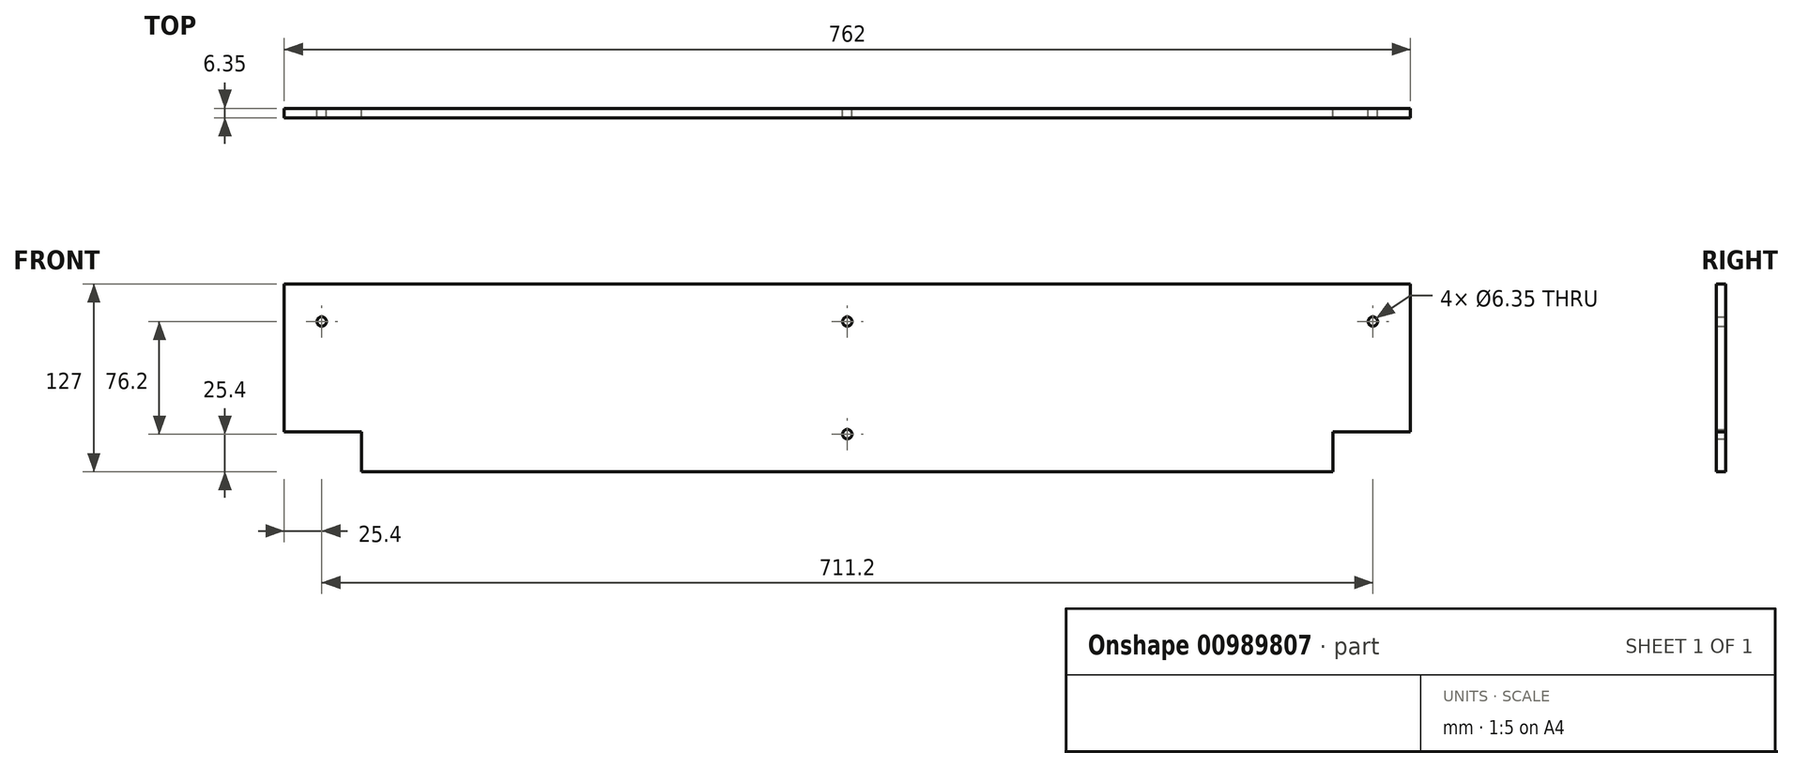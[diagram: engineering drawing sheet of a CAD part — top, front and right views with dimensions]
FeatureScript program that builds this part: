
annotation { "Feature Type Name" : "Feature", "Feature Type Description" : "" }
export const myFeature = defineFeature(function(context is Context, id is Id, definition is map)
    precondition{}
    {
        {
            var Q0;
            Q0=qCreatedBy(makeId("Front.planeOp"),FACE);
            var sketch = newSketch(context, id + "F0", { "sketchPlane" : qUnion([Q0])});
            skLineSegment(sketch, "E0.bottom", {"start": v(-381, 63.5) * mm, "end": v(381, 63.5) * mm});
            skLineSegment(sketch, "E0.top", {"start": v(-328.61, -63.5) * mm, "end": v(328.61, -63.5) * mm});
            skLineSegment(sketch, "E0.left", {"start": v(-381, 63.5) * mm, "end": v(-381, -36.51) * mm});
            skLineSegment(sketch, "E0.right", {"start": v(381, 63.5) * mm, "end": v(381, -36.51) * mm});
            skLineSegment(sketch, "E1.top", {"start": v(-381, -36.51) * mm, "end": v(-328.61, -36.51) * mm});
            skLineSegment(sketch, "E1.right", {"start": v(-328.61, -63.5) * mm, "end": v(-328.61, -36.51) * mm});
            skLineSegment(sketch, "E2.1.0.0", {"start": v(328.61, -36.51) * mm, "end": v(381, -36.51) * mm});
            skLineSegment(sketch, "E2.1.0.1", {"start": v(328.61, -63.5) * mm, "end": v(328.61, -36.51) * mm});
            skLineSegment(sketch, "E2.direction1", {"start": v(-381, -36.51) * mm, "end": v(328.61, -36.51) * mm, "construction": true});
            skPoint(sketch, "E3.orphan", {"position": v(328.61, -63.5) * mm});
            skCircle(sketch, "E4", {"center": v(-355.6, 38.1) * mm, "radius": 3.18 * mm});
            skCircle(sketch, "E5.1.0.0", {"center": v(0, 38.1) * mm, "radius": 3.18 * mm});
            skCircle(sketch, "E5.2.0.0", {"center": v(355.6, 38.1) * mm, "radius": 3.18 * mm});
            skLineSegment(sketch, "E5.direction1", {"start": v(-355.6, 38.1) * mm, "end": v(0, 38.1) * mm, "construction": true});
            skCircle(sketch, "E6.0.1.0", {"center": v(0, -38.1) * mm, "radius": 3.18 * mm});
            skLineSegment(sketch, "E6.direction1", {"start": v(0, 38.1) * mm, "end": v(25.4, 38.1) * mm, "construction": true});
            skLineSegment(sketch, "E6.direction2", {"start": v(0, 38.1) * mm, "end": v(0, -38.1) * mm, "construction": true});
            skSolve(sketch);
        }
        {
            var Q0;
            Q0=makeQuery(id+"F0.imprint","IMPRINT",FACE,{"disambiguationData":[TD([[makeQuery(id+"F0.imprint","IMPRINT",EDGE,{"derivedFrom":sQuery(id+"F0.wireOp",EDGE,"E0.bottom")}),-1.0]])]});
            extrude(context, id + "F1", {"entities" : qUnion([Q0]), "depth" : 6.35 * mm, "offsetDistance" : 25.4 * mm});
        }
    });
